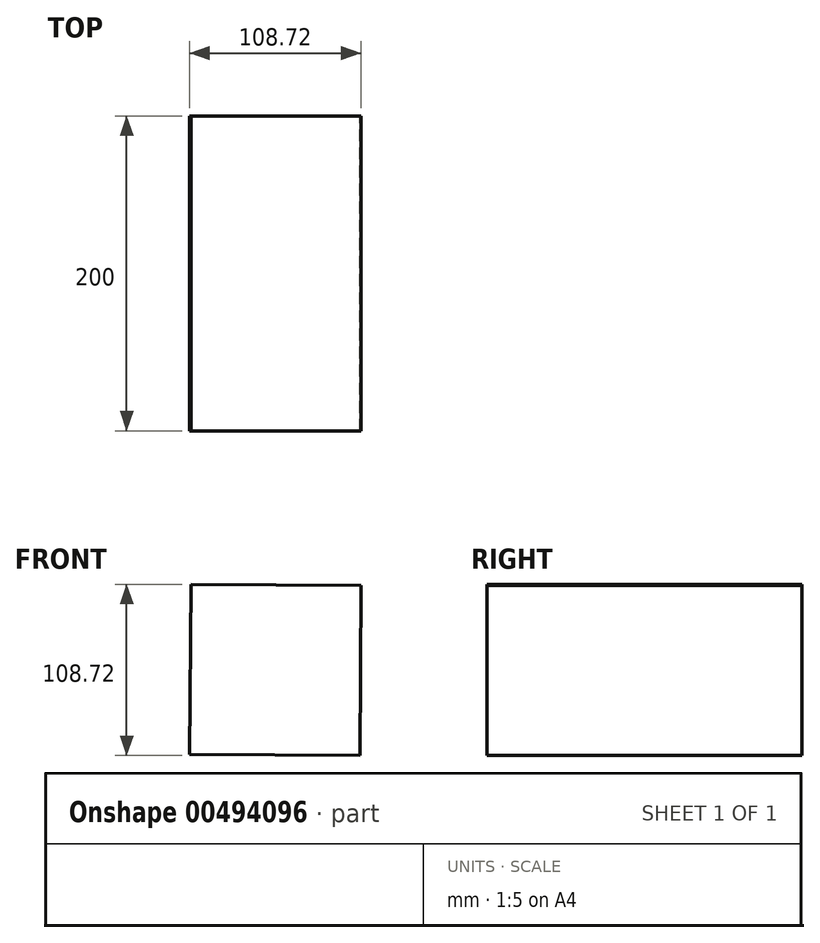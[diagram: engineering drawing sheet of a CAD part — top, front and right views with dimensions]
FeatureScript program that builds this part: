
annotation { "Feature Type Name" : "Feature", "Feature Type Description" : "" }
export const myFeature = defineFeature(function(context is Context, id is Id, definition is map)
    precondition{}
    {
        {
            var Q0;
            Q0=qCreatedBy(makeId("Front.planeOp"),FACE);
            var sketch = newSketch(context, id + "F0", { "sketchPlane" : qUnion([Q0])});
            skCircle(sketch, "E0.cCircle", {"center": v(0, 0) * mm, "radius": 76.38 * mm, "construction": true});
            skLineSegment(sketch, "E0.0", {"start": v(54.36, 53.65) * mm, "end": v(53.65, -54.36) * mm});
            skLineSegment(sketch, "E0.1", {"start": v(53.65, -54.36) * mm, "end": v(-54.36, -53.65) * mm});
            skLineSegment(sketch, "E0.2", {"start": v(-54.36, -53.65) * mm, "end": v(-53.65, 54.36) * mm});
            skLineSegment(sketch, "E0.3", {"start": v(-53.65, 54.36) * mm, "end": v(54.36, 53.65) * mm});
            skSolve(sketch);
        }
        {
            var Q0;
            Q0 = qSketchRegion(id + "F0", true);
            extrude(context, id + "F1", {"entities" : qUnion([Q0]), "depth" : 200 * mm});
        }
    });
